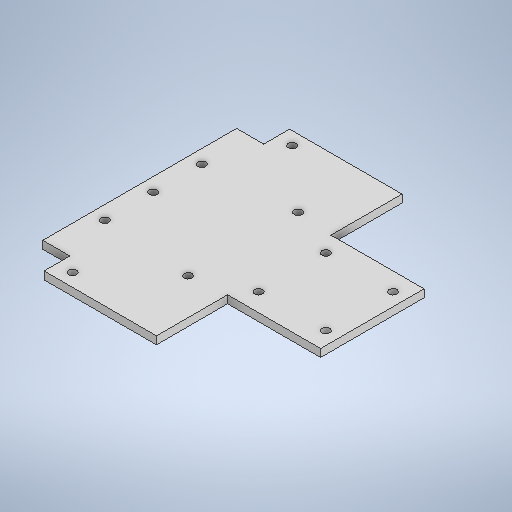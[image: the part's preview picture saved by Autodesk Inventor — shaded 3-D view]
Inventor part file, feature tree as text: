
AUTODESK INVENTOR PART (.ipt)
format: ipt  version: 2025.1 (Build 291241020, 241B)  size: 305,152 bytes
history: native  units: in
note: dims shown in document units (in); Inventor stores cm internally (conversion verified against a paired STEP export)
features: extrude x1, sketch x1
ambient origin geometry x8: Origin, YZ Plane, XZ Plane, XY Plane, X Axis, Y Axis, Z Axis, Center Point
bodies: Body1 (feature_tree)
feature tree (2):
  extrude  "Extrusion2"  Depth=0.1181in
  sketch  "Sketch1"  dims[d2=0.2362in d3=0.4724in d4=0.5512in d5=0.5512in d6=1.4173in d7=1.4173in d13=0.122in d14=0.122in d15=0.122in d17=0.4134in d19=0.4134in d22=0.122in d23=0.122in d27=0.122in d28=0.122in d32=0.122in d33=0.122in d34=0.122in d37=0.1181in d38=0.0in]
